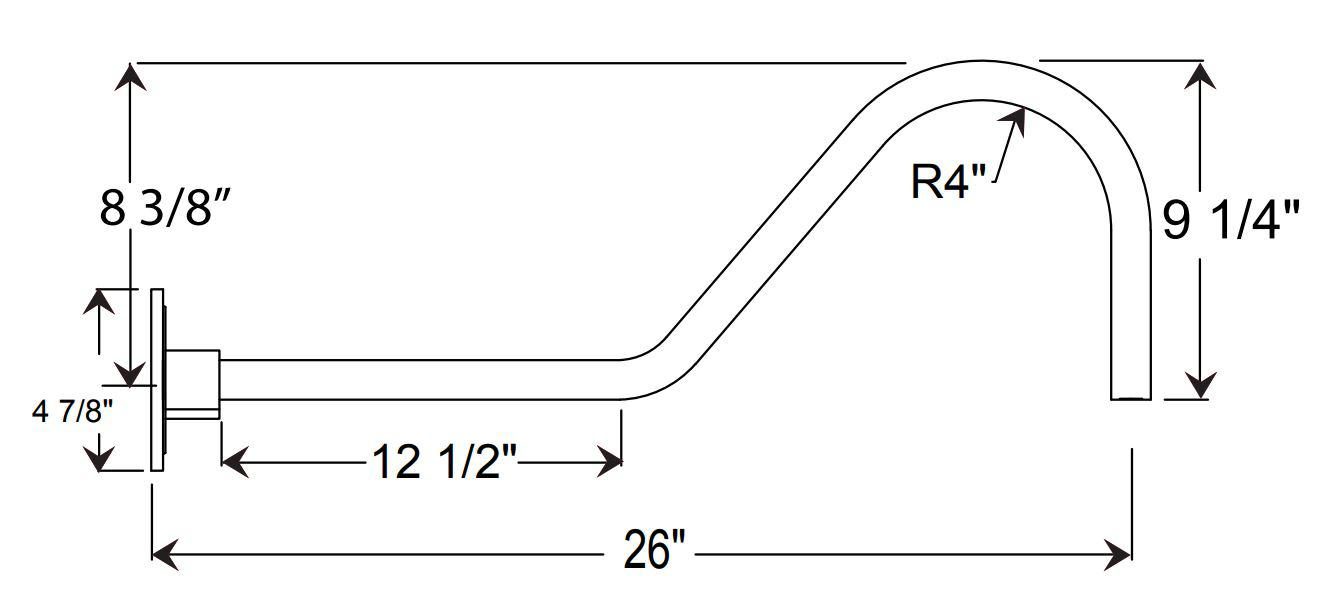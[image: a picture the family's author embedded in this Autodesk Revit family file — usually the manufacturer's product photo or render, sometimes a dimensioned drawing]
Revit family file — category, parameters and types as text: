
# Revit family: BELL(8,10,14) MB
name_source: partatom
category: Lighting Fixtures
units: mm (PartAtom-declared; Revit-internal decimal feet)

## family parameters
Always vertical = Yes
Cut with Voids When Loaded = No
Light Source = Yes
OmniClass Number = 23.80.70.00
OmniClass Title = Lighting
Part Type = Normal
Room Calculation Point = No
Round Connector Dimension = Use Diameter
Shared = No
Work Plane-Based = No

## types (4) — shared parameters
Body Colour = Spun aluminium
Body Material = body
CRI = >90
Color Filter = 16777215
Construction Material = Heavy Duty spun aluminum.
Default Elevation = 0' - 0"
Description = 120-277 Voltage
Dimming = 1%
Dimming Lamp Color Temperature Shift = <None>
Efficiency = 65-125 lumens per watt
Lamp = MB
Life = L70 50,000 hours
Load Classification = Lighting
Manufacturer = ANP Lighting
Photometric Web File = generic.ies
Power Factor = 1
Tilt Angle = 90.00°
URL = https://www.anplighting.com
Voltage = 277 V
Warranty = 5 year limited warranty

## per-type parameters (varying)
| type | Apparent Load | BELL10 | BELL12 | BELL14 | BELL8 | Fixture Diameter | Fixture Height | Wattage Comments | Weight |
| BEL08 | 100 VA | No | No | No | Yes | 0' - 8" | 0' - 6 1/2" | 100W Max | 1.5 lbs |
| BEL10 | 100 VA | Yes | No | No | No | 0' - 10" | 0' - 7 1/2" | 100W Max | 2 lbs |
| BEL12 | 200 VA | No | Yes | No | No | 1' - 0" | 0' - 9" | 200W Max | 2.5 lbs |
| BEL14 | 200 VA | No | No | Yes | No | 1' - 2" | 0' - 10 1/2" | 200W Max | 3.0 lbs |

note: column(s) folded — value = type name in every type: Model

## geometry (parser evidence)
native form markers: Sweep x35
no freeform markers — native parametric forms only
